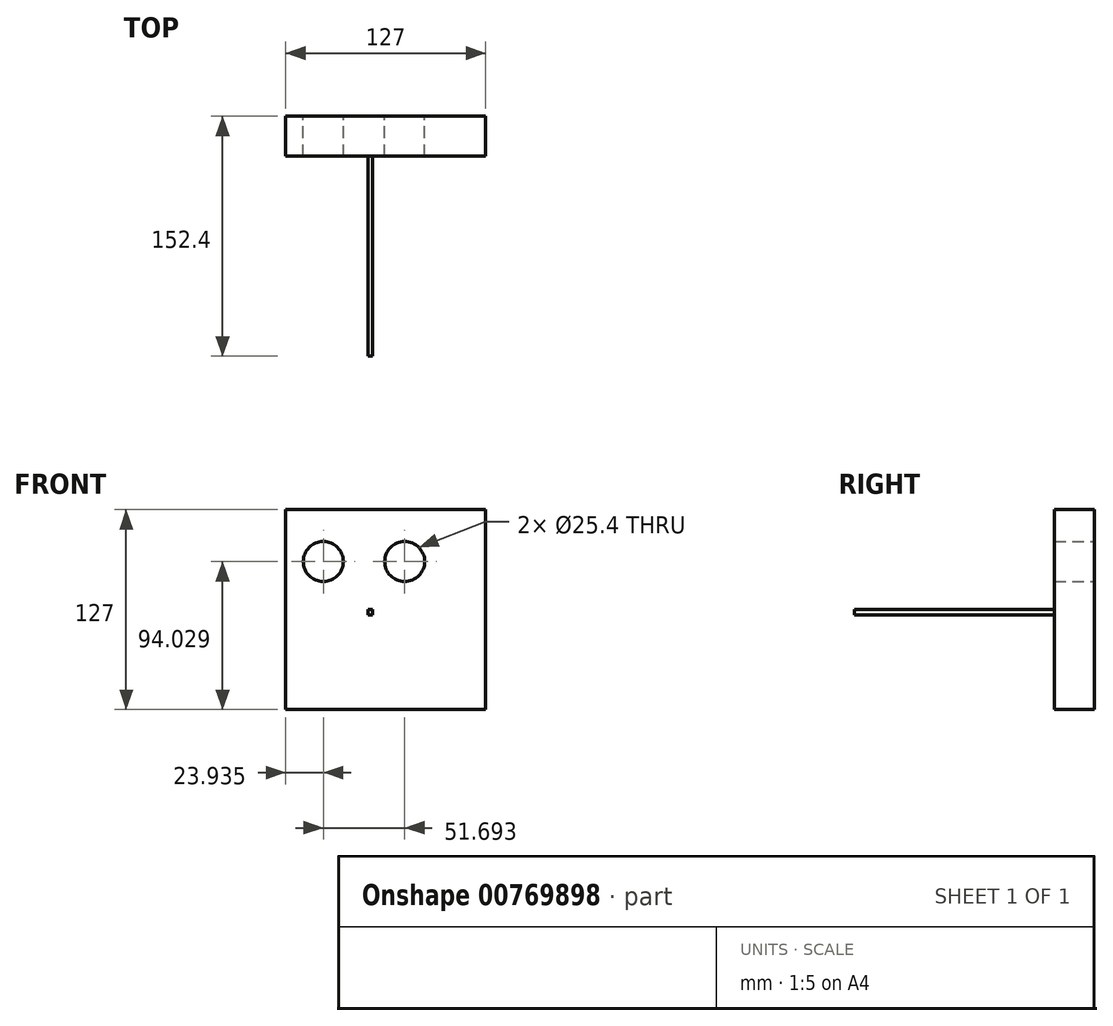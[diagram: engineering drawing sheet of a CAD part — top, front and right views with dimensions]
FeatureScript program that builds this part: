
annotation { "Feature Type Name" : "Feature", "Feature Type Description" : "" }
export const myFeature = defineFeature(function(context is Context, id is Id, definition is map)
    precondition{}
    {
        {
            var Q0;
            Q0=qCreatedBy(makeId("Front.planeOp"),FACE);
            var sketch = newSketch(context, id + "F0", { "sketchPlane" : qUnion([Q0])});
            skLineSegment(sketch, "E0.bottom", {"start": v(-104.62, 63.5) * mm, "end": v(22.38, 63.5) * mm});
            skLineSegment(sketch, "E0.top", {"start": v(-104.62, -63.5) * mm, "end": v(22.38, -63.5) * mm});
            skLineSegment(sketch, "E0.left", {"start": v(-104.62, 63.5) * mm, "end": v(-104.62, -63.5) * mm});
            skLineSegment(sketch, "E0.right", {"start": v(22.38, 63.5) * mm, "end": v(22.38, -63.5) * mm});
            skPoint(sketch, "E1", {"position": v(-44.16, 0) * mm});
            skSolve(sketch);
        }
        {
            var Q0;
            Q0=makeQuery(id+"F0.imprint","IMPRINT",FACE,{"disambiguationData":[TD([[makeQuery(id+"F0.imprint","IMPRINT",EDGE,{"derivedFrom":sQuery(id+"F0.wireOp",EDGE,"E0.bottom")}),-1.0]])]});
            var sketch = newSketch(context, id + "F1", { "sketchPlane" : qUnion([Q0])});
            skCircle(sketch, "E2", {"center": v(-80.68, 30.53) * mm, "radius": 12.7 * mm});
            skCircle(sketch, "E3", {"center": v(-29, 30.53) * mm, "radius": 12.7 * mm});
            skSolve(sketch);
        }
        {
            var Q0;
            Q0=makeQuery(id+"F1.imprint","IMPRINT",FACE,{"disambiguationData":[TD([[makeQuery(id+"F1.imprint","IMPRINT",EDGE,{"derivedFrom":sQuery(id+"F1.wireOp",EDGE,"E2")}),-1.0]])]});
            extrude(context, id + "F2", {"entities" : qUnion([Q0]), "depth" : 25.4 * mm, "offsetDistance" : 25.4 * mm});
        }
        {
            var Q0;
            Q0=makeQuery(id+"F2.opExtrude","CAP_FACE",FACE,{"disambiguationData":[OSD([sQuery(id+"F0.wireOp",EDGE,"E0.bottom"),sQuery(id+"F0.wireOp",EDGE,"E0.top"),sQuery(id+"F0.wireOp",EDGE,"E0.left"),sQuery(id+"F0.wireOp",EDGE,"E0.right"),sQuery(id+"F1.wireOp",EDGE,"E2"),sQuery(id+"F1.wireOp",EDGE,"E3")])],"isStart":false});
            var sketch = newSketch(context, id + "F3", { "sketchPlane" : qUnion([Q0])});
            skPoint(sketch, "E4.firstSnap0", {"position": v(-104.62, 0) * mm});
            skLineSegment(sketch, "E4.bottom", {"start": v(-52.32, 0) * mm, "end": v(-49.57, 0) * mm});
            skLineSegment(sketch, "E4.top", {"start": v(-52.32, -3.43) * mm, "end": v(-49.57, -3.43) * mm});
            skLineSegment(sketch, "E4.left", {"start": v(-52.32, 0) * mm, "end": v(-52.32, -3.43) * mm});
            skLineSegment(sketch, "E4.right", {"start": v(-49.57, 0) * mm, "end": v(-49.57, -3.43) * mm});
            skSolve(sketch);
        }
        {
            var Q0;
            Q0 = qSketchRegion(id + "F3", true);
            extrude(context, id + "F4", {"entities" : qUnion([Q0]), "operationType" : NewBodyOperationType.ADD, "depth" : 127 * mm, "offsetDistance" : 25.4 * mm});
        }
    });
